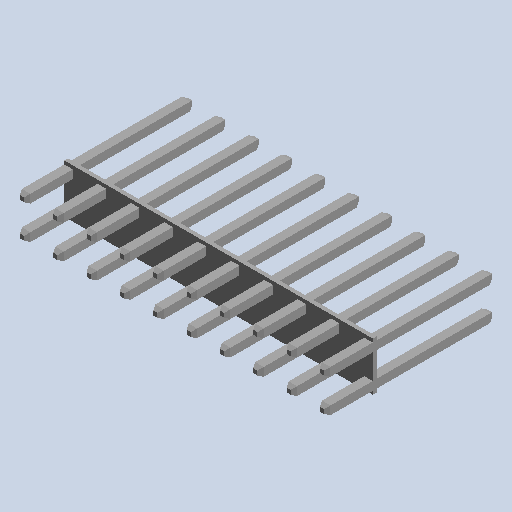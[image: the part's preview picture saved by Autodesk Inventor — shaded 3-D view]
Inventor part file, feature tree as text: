
AUTODESK INVENTOR PART (.ipt)
format: ipt  version: 2024.2 (Build 282272000, 272)  size: 557,568 bytes
history: native  units: mm (DEFAULTED — no unit token found)
features: other x7, extrude x2, sketch x2
ambient origin geometry x8: Origin, YZ Plane, XZ Plane, XY Plane, X Axis, Y Axis, Z Axis, Center Point
bodies: Solid1 (feature_tree)
feature tree (11):
  extrude  "Extrusion1"  Depth=18.507964mm TaperAngle=0.0deg
  extrude  "Extrusion2"  [1 undecoded]
  other  "0_XY"
  other  "0_YZ"
  other  "0_ZX"
  other  "0_X"
  other  "0_Y"
  other  "0_Z"
  other  "0_Center"
  sketch  "Sketch_2"
  sketch  "Sketch_1"  dims[d0=18.507964mm d1=0.0mm d2=15.24mm d3=0.0mm]
note: 1 required parameter value undecoded (feature->parameter linkage not recoverable at this tier; creation-order binding heuristic only, values carry confidence <= 0.55)
